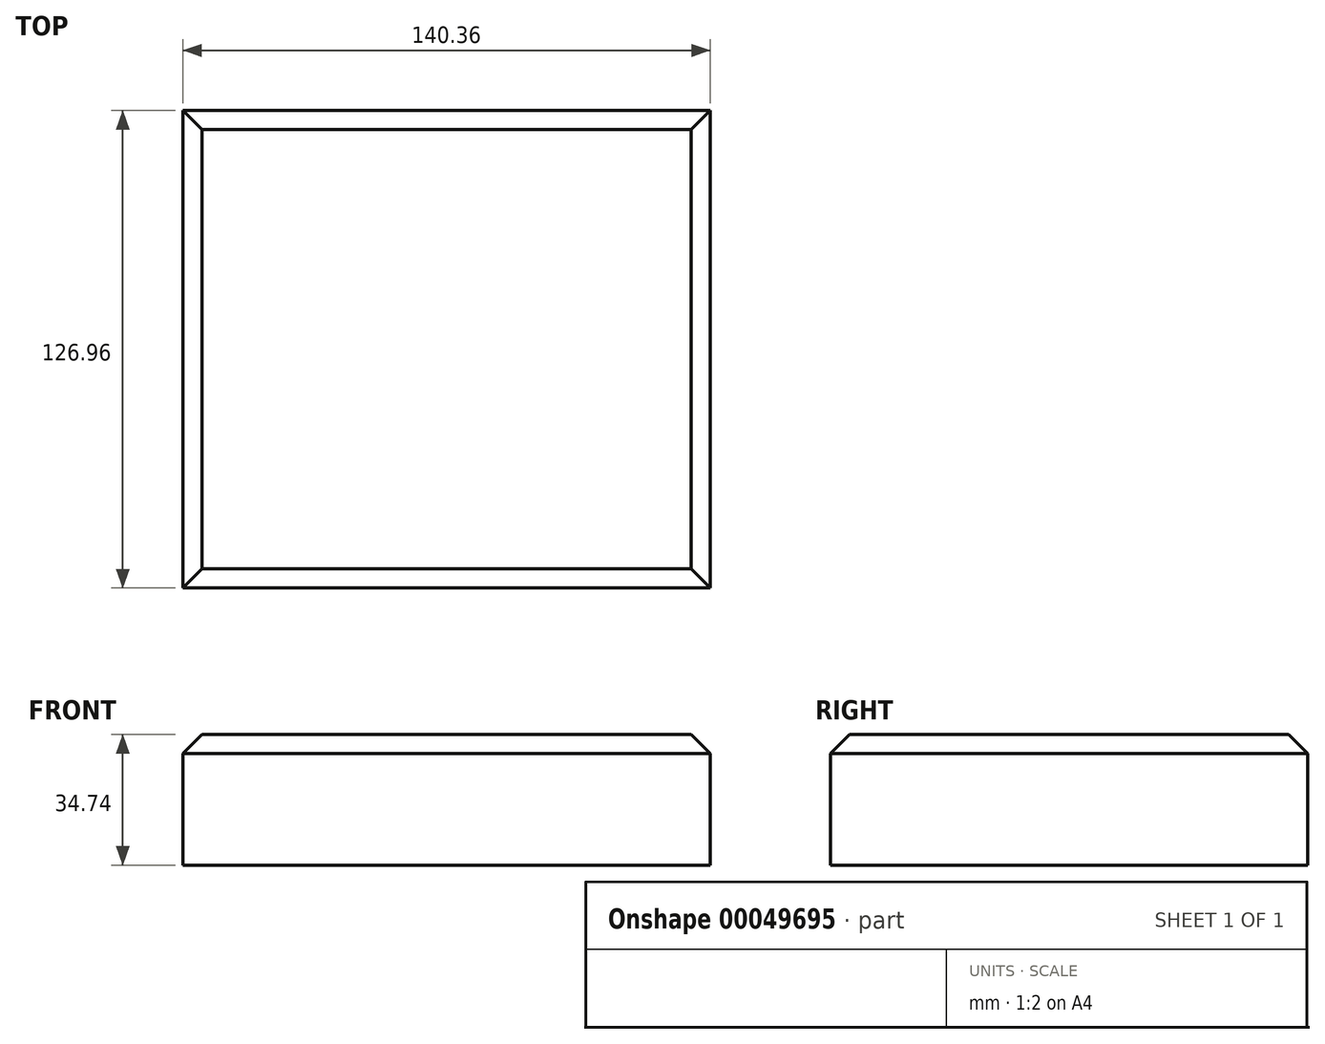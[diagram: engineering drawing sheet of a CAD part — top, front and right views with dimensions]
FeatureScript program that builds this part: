
annotation { "Feature Type Name" : "Feature", "Feature Type Description" : "" }
export const myFeature = defineFeature(function(context is Context, id is Id, definition is map)
    precondition{}
    {
        {
            var Q0;
            Q0=qCreatedBy(makeId("Top.planeOp"),FACE);
            var sketch = newSketch(context, id + "F0", { "sketchPlane" : qUnion([Q0])});
            skLineSegment(sketch, "E0.rect.bottom", {"start": v(70.18, -63.48) * mm, "end": v(-70.18, -63.48) * mm});
            skLineSegment(sketch, "E0.rect.top", {"start": v(70.18, 63.48) * mm, "end": v(-70.18, 63.48) * mm});
            skLineSegment(sketch, "E0.rect.left", {"start": v(70.18, -63.48) * mm, "end": v(70.18, 63.48) * mm});
            skLineSegment(sketch, "E0.rect.right", {"start": v(-70.18, -63.48) * mm, "end": v(-70.18, 63.48) * mm});
            skPoint(sketch, "E0.rect.middle", {"position": v(0, 0) * mm});
            skSolve(sketch);
        }
        {
            var Q0;
            Q0=makeQuery(id+"F0.imprint","IMPRINT",FACE,{"disambiguationData":[TD([[makeQuery(id+"F0.imprint","IMPRINT",EDGE,{"derivedFrom":sQuery(id+"F0.wireOp",EDGE,"E0.rect.bottom")}),-1.0]])]});
            extrude(context, id + "F1", {"entities" : qUnion([Q0]), "depth" : 34.74 * mm});
        }
        {
            var Q0;
            Q0=makeQuery(id+"F1.opExtrude","CAP_EDGE",EDGE,{"disambiguationData":[OSD([sQuery(id+"F0.wireOp",EDGE,"E0.rect.bottom")])],"isStart":false});
            var Q1;
            Q1=makeQuery(id+"F1.opExtrude","CAP_EDGE",EDGE,{"disambiguationData":[OSD([sQuery(id+"F0.wireOp",EDGE,"E0.rect.right")])],"isStart":false});
            var Q2;
            Q2=makeQuery(id+"F1.opExtrude","CAP_EDGE",EDGE,{"disambiguationData":[OSD([sQuery(id+"F0.wireOp",EDGE,"E0.rect.top")])],"isStart":false});
            var Q3;
            Q3=makeQuery(id+"F1.opExtrude","CAP_EDGE",EDGE,{"disambiguationData":[OSD([sQuery(id+"F0.wireOp",EDGE,"E0.rect.left")])],"isStart":false});
            chamfer(context, id + "F2", {"entities" : qUnion([Q0, Q1, Q2, Q3]), "width" : 5.08 * mm, "tangentPropagation" : true});
        }
    });
